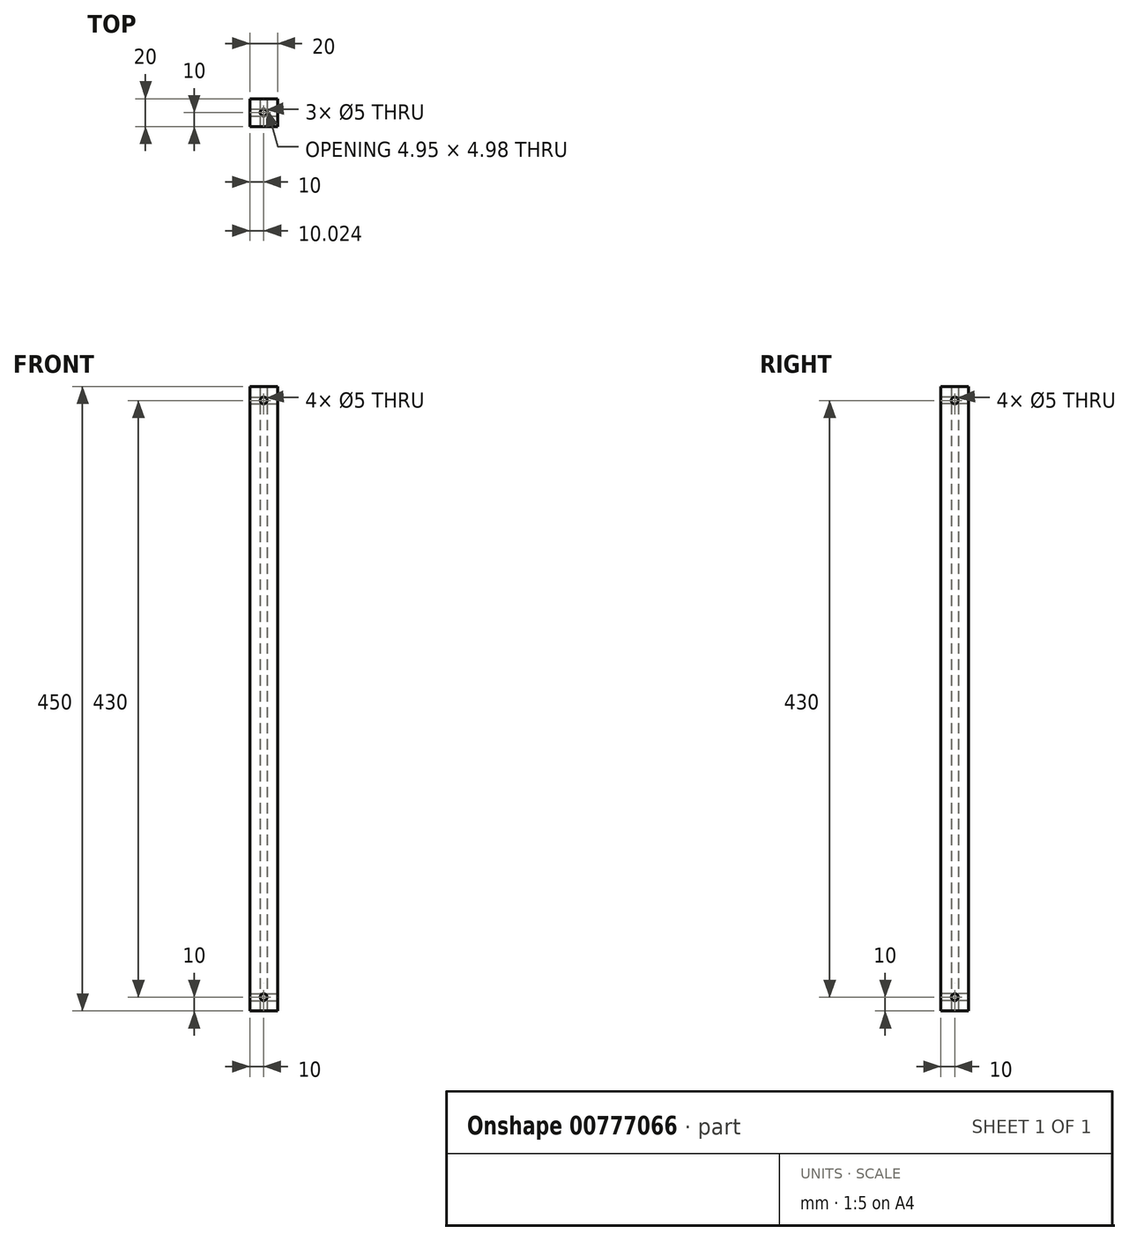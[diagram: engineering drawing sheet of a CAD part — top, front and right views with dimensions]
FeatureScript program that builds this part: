
annotation { "Feature Type Name" : "Feature", "Feature Type Description" : "" }
export const myFeature = defineFeature(function(context is Context, id is Id, definition is map)
    precondition{}
    {
        {
            var Q0;
            Q0=qCreatedBy(makeId("Top.planeOp"),FACE);
            var sketch = newSketch(context, id + "F0", { "sketchPlane" : qUnion([Q0])});
            skLineSegment(sketch, "E0.bottom", {"start": v(-10, 10) * mm, "end": v(10, 10) * mm});
            skLineSegment(sketch, "E0.top", {"start": v(-10, -10) * mm, "end": v(10, -10) * mm});
            skLineSegment(sketch, "E0.left", {"start": v(-10, 10) * mm, "end": v(-10, -10) * mm});
            skLineSegment(sketch, "E0.right", {"start": v(10, 10) * mm, "end": v(10, -10) * mm});
            skCircle(sketch, "E1", {"center": v(0, 0) * mm, "radius": 2.5 * mm});
            skSolve(sketch);
        }
        {
            var Q0;
            Q0=qSketchRegion(id+"F0",true);
            extrude(context, id + "F1", {"entities" : qUnion([Q0]), "depth" : (500 - 50) * mm, "offsetDistance" : 25 * mm});
        }
        {
            var Q0;
            Q0=makeQuery(id+"F1.opExtrude","SWEPT_FACE",FACE,{"disambiguationData":[OSD([sQuery(id+"F0.wireOp",EDGE,"E0.right")])]});
            var sketch = newSketch(context, id + "F2", { "sketchPlane" : qUnion([Q0])});
            skCircle(sketch, "E2", {"center": v(0, 10) * mm, "radius": 2.5 * mm});
            skCircle(sketch, "E3", {"center": v(0, 440) * mm, "radius": 2.5 * mm});
            skSolve(sketch);
        }
        {
            var Q0;
            Q0=qSketchRegion(id+"F2",true);
            extrude(context, id + "F3", {"entities" : qUnion([Q0]), "operationType" : NewBodyOperationType.REMOVE, "endBound" : BoundingType.THROUGH_ALL, "oppositeDirection" : true, "depth" : 25 * mm});
        }
        {
            var Q0;
            Q0=makeQuery(id+"F1.opExtrude","SWEPT_FACE",FACE,{"disambiguationData":[OSD([sQuery(id+"F0.wireOp",EDGE,"E0.top")])]});
            var sketch = newSketch(context, id + "F4", { "sketchPlane" : qUnion([Q0])});
            skCircle(sketch, "E4", {"center": v(0, 440) * mm, "radius": 2.5 * mm});
            skCircle(sketch, "E5", {"center": v(0, 10) * mm, "radius": 2.5 * mm});
            skSolve(sketch);
        }
        {
            var Q0;
            Q0=qSketchRegion(id+"F4",true);
            extrude(context, id + "F5", {"entities" : qUnion([Q0]), "operationType" : NewBodyOperationType.REMOVE, "endBound" : BoundingType.THROUGH_ALL, "oppositeDirection" : true, "depth" : 25 * mm});
        }
    });
